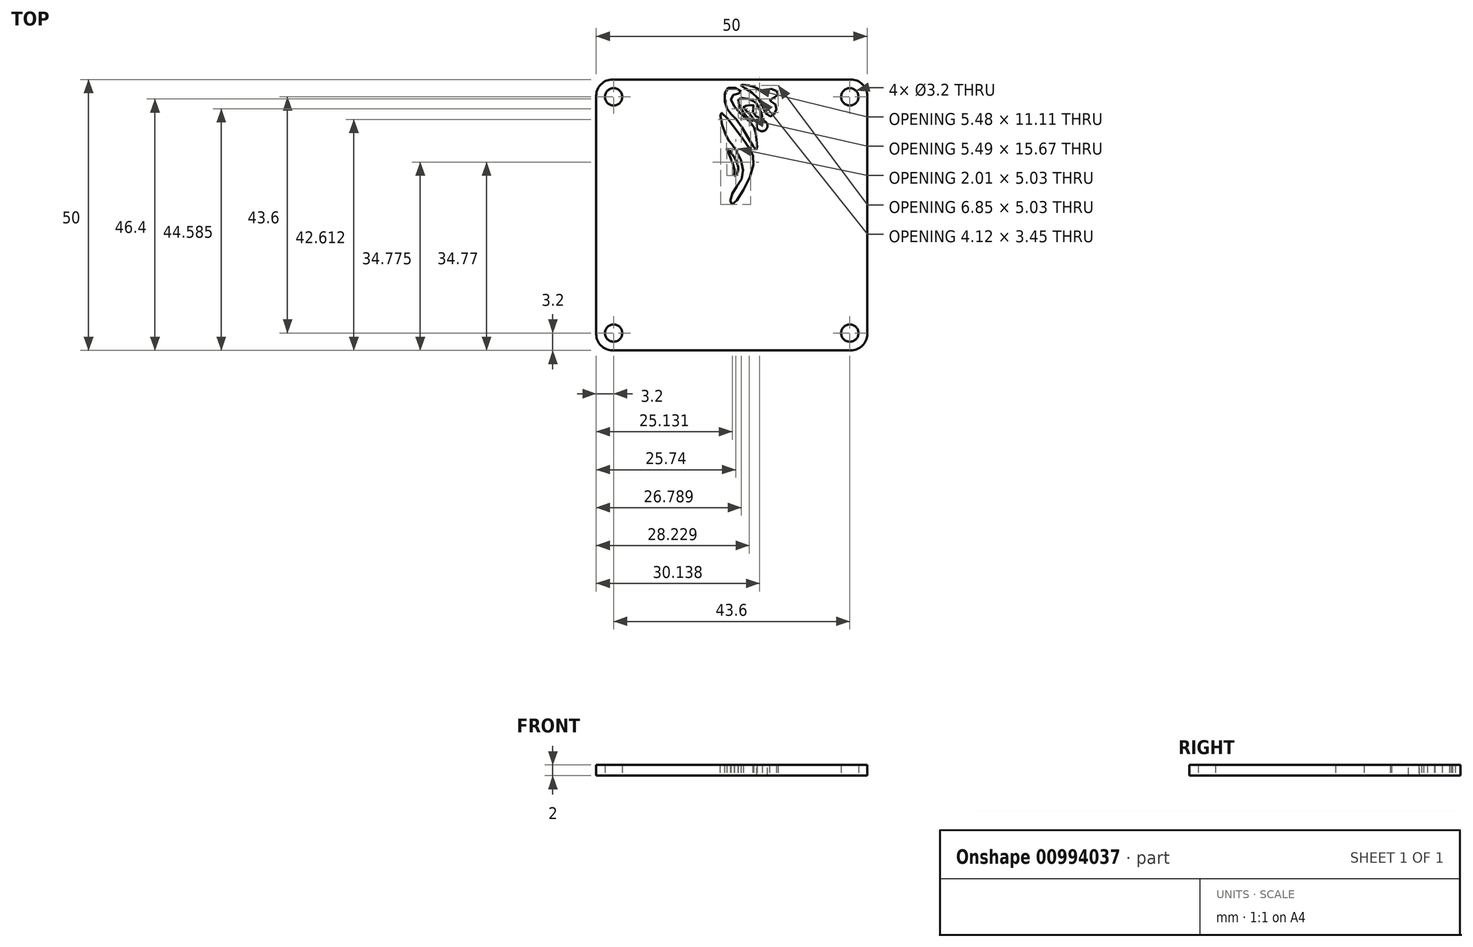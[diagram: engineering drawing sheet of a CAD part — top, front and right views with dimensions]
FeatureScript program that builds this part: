
annotation { "Feature Type Name" : "Feature", "Feature Type Description" : "" }
export const myFeature = defineFeature(function(context is Context, id is Id, definition is map)
    precondition{}
    {
        {
            var Q0;
            Q0=qCreatedBy(makeId("Top.planeOp"),FACE);
            var sketch = newSketch(context, id + "F0", { "sketchPlane" : qUnion([Q0])});
            skLineSegment(sketch, "E0.bottom", {"start": v(-25, 25) * mm, "end": v(25, 25) * mm});
            skLineSegment(sketch, "E0.top", {"start": v(-25, -25) * mm, "end": v(25, -25) * mm});
            skLineSegment(sketch, "E0.left", {"start": v(-25, 25) * mm, "end": v(-25, -25) * mm});
            skLineSegment(sketch, "E0.right", {"start": v(25, 25) * mm, "end": v(25, -25) * mm});
            skPoint(sketch, "E1", {"position": v(0, 25) * mm});
            skPoint(sketch, "E2", {"position": v(25, 0) * mm});
            skPoint(sketch, "E3", {"position": v(-21.8, 21.8) * mm});
            skPoint(sketch, "E4.1.0", {"position": v(-21.8, -21.8) * mm});
            skPoint(sketch, "E4.2.0", {"position": v(21.8, -21.8) * mm});
            skPoint(sketch, "E4.center", {"position": v(0, 0) * mm});
            skPoint(sketch, "E5.0.3.0", {"position": v(21.8, 21.8) * mm});
            skLineSegment(sketch, "E6", {"start": v(0, 25) * mm, "end": v(0, -25) * mm, "construction": true});
            skLineSegment(sketch, "E7", {"start": v(25, 0) * mm, "end": v(-25, 0) * mm, "construction": true});
            skSolve(sketch);
        }
        {
            var Q0;
            Q0=makeQuery(id+"F0.imprint","IMPRINT",FACE,{"disambiguationData":[TD([[makeQuery(id+"F0.imprint","IMPRINT",EDGE,{"derivedFrom":sQuery(id+"F0.wireOp",EDGE,"E0.bottom")}),-1.0]])]});
            extrude(context, id + "F1", {"entities" : qUnion([Q0]), "depth" : 2 * mm, "offsetDistance" : 25 * mm});
        }
        {
            var Q0;
            Q0=sQuery(id+"F0.wireOp",VERTEX,"E3");
            var Q1;
            Q1=sQuery(id+"F0.wireOp",VERTEX,"E5.0.3.0");
            var Q2;
            Q2=sQuery(id+"F0.wireOp",VERTEX,"E4.2.0");
            var Q3;
            Q3=sQuery(id+"F0.wireOp",VERTEX,"E4.1.0");
            var Q4;
            Q4=makeQuery(id+"F1.opExtrude","SWEPT_BODY",BODY,{"disambiguationData":[OSD([sQuery(id+"F0.wireOp",EDGE,"E0.bottom"),sQuery(id+"F0.wireOp",EDGE,"E0.top"),sQuery(id+"F0.wireOp",EDGE,"E0.left"),sQuery(id+"F0.wireOp",EDGE,"E0.right")])]});
            hole(context, id + "F2", {"style" : HoleStyle.SIMPLE, "endStyle" : HoleEndStyle.THROUGH, "oppositeDirection" : true, "standardTappedOrClearance" : lookupTablePath({ "fit" : "Close", "standard" : "ISO", "size" : "M3", "type" : "Clearance" }), "standardBlindInLast" : lookupTablePath({ "fit" : "Close", "standard" : "ISO", "engagement" : "75%", "pitch" : "0.5 mm", "size" : "M3", "type" : "Clearance & tapped" }), "holeDiameter" : 3.2 * mm, "majorDiameter" : 5 * mm, "isTappedThrough" : true, "tappedDepth" : 12 * mm, "tapClearance" : 3, "startFromSketch" : true, "locations" : qUnion([Q0, Q1, Q2, Q3]), "scope" : qUnion([Q4])});
        }
        {
            var Q0;
            Q0=makeQuery(id+"F1.opExtrude","CAP_FACE",FACE,{"disambiguationData":[OSD([sQuery(id+"F0.wireOp",EDGE,"E0.bottom"),sQuery(id+"F0.wireOp",EDGE,"E0.top"),sQuery(id+"F0.wireOp",EDGE,"E0.left"),sQuery(id+"F0.wireOp",EDGE,"E0.right")])],"isStart":false});
            var sketch = newSketch(context, id + "F3", { "sketchPlane" : qUnion([Q0])});
            skFitSpline(sketch, "E8", {"points": [v(0.03, 1.94) * mm, v(3.96, 8.95) * mm, v(2.06, 14.02) * mm, v(-2.07, 18.85) * mm, v(-0.8, 14.09) * mm, v(0, 13.14) * mm, v(2.12, 7.8) * mm, v(0, 3.76) * mm, v(0.03, 1.94) * mm]});
            skFitSpline(sketch, "E9", {"points": [v(4.53, 12.06) * mm, v(1.3, 17.07) * mm, v(-1.05, 20.05) * mm, v(-0.55, 23.48) * mm, v(1.74, 22.72) * mm, v(0, 21.9) * mm, v(1.61, 18.72) * mm, v(3.96, 16.45) * mm, v(4.6, 13.64) * mm, v(4.53, 12.06) * mm]});
            skFitSpline(sketch, "E10", {"points": [v(-0.87, 12.29) * mm, v(1.22, 8.65) * mm, v(0.53, 7.25) * mm, v(0.43, 8.65) * mm, v(-0.87, 12.29) * mm]});
            skPoint(sketch, "E11.0", {"position": v(0, 0) * mm});
            skFitSpline(sketch, "E12", {"points": [v(1.17, 21.3) * mm, v(3.73, 21.15) * mm, v(4.86, 20.08) * mm, v(5.55, 17.89) * mm, v(3.95, 18.85) * mm, v(4.06, 20.19) * mm, v(2.88, 20.19) * mm, v(2.19, 19.87) * mm, v(4, 17.78) * mm, v(3.68, 17.35) * mm, v(1.17, 21.3) * mm]});
            skFitSpline(sketch, "E13", {"points": [v(4.38, 23.55) * mm, v(1.7, 23.98) * mm, v(4.48, 21.95) * mm, v(6.3, 18.85) * mm, v(7.47, 18.26) * mm, v(8.12, 20.35) * mm, v(7, 21.15) * mm, v(8.54, 22.27) * mm, v(7.26, 23.29) * mm, v(5.6, 22.96) * mm, v(4.38, 23.55) * mm]});
            skCircle(sketch, "E14", {"center": v(5.6, 16.45) * mm, "radius": 1 * mm});
            skSolve(sketch);
        }
        {
            var Q0;
            Q0=makeQuery(id+"F3.imprint","IMPRINT",FACE,{"disambiguationData":[TD([[makeQuery(id+"F3.imprint","IMPRINT",EDGE,{"derivedFrom":sQuery(id+"F3.wireOp",EDGE,"E8")}),1.0]])]});
            var Q1;
            Q1=makeQuery(id+"F3.imprint","IMPRINT",FACE,{"disambiguationData":[TD([[makeQuery(id+"F3.imprint","IMPRINT",EDGE,{"derivedFrom":sQuery(id+"F3.wireOp",EDGE,"E9")}),-1.0]])]});
            var Q2;
            Q2=makeQuery(id+"F3.imprint","IMPRINT",FACE,{"disambiguationData":[TD([[makeQuery(id+"F3.imprint","IMPRINT",EDGE,{"derivedFrom":sQuery(id+"F3.wireOp",EDGE,"E10")}),-1.0]])]});
            var Q3;
            Q3=makeQuery(id+"F3.imprint","IMPRINT",FACE,{"disambiguationData":[TD([[makeQuery(id+"F3.imprint","IMPRINT",EDGE,{"derivedFrom":sQuery(id+"F3.wireOp",EDGE,"0e831b12-4cfc-4eb4-9b18-7b789f5edcee")}),1.0]])]});
            var Q4;
            Q4=makeQuery(id+"F3.imprint","IMPRINT",FACE,{"disambiguationData":[TD([[makeQuery(id+"F3.imprint","IMPRINT",EDGE,{"derivedFrom":sQuery(id+"F3.wireOp",EDGE,"E12")}),-1.0]])]});
            var Q5;
            Q5=makeQuery(id+"F3.imprint","IMPRINT",FACE,{"disambiguationData":[TD([[makeQuery(id+"F3.imprint","IMPRINT",EDGE,{"derivedFrom":sQuery(id+"F3.wireOp",EDGE,"E13")}),1.0]])]});
            var Q6;
            Q6=makeQuery(id+"F3.imprint","IMPRINT",FACE,{"disambiguationData":[TD([[makeQuery(id+"F3.imprint","IMPRINT",EDGE,{"derivedFrom":sQuery(id+"F3.wireOp",EDGE,"E14")}),1.0]])]});
            extrude(context, id + "F4", {"entities" : qUnion([Q0, Q1, Q2, Q3, Q4, Q5, Q6]), "operationType" : NewBodyOperationType.REMOVE, "endBound" : BoundingType.THROUGH_ALL, "oppositeDirection" : true, "depth" : 25 * mm, "offsetDistance" : 25 * mm});
        }
        {
            var Q0;
            Q0=qCreatedBy(makeId("Right.planeOp"),FACE);
            var sketch = newSketch(context, id + "F5", { "sketchPlane" : qUnion([Q0])});
            skPoint(sketch, "E15.0", {"position": v(0, 0) * mm});
            skPoint(sketch, "E16.0", {"position": v(0, 2) * mm});
            skLineSegment(sketch, "E17.0", {"start": v(0, 0) * mm, "end": v(0, 2) * mm});
            skSolve(sketch);
        }
        {
            var Q0;
            Q0=makeQuery(id+"F1.opExtrude","SWEPT_EDGE",EDGE,{"disambiguationData":[OSD([sQuery(id+"F0.wireOp",EDGE,"E0.bottom"),sQuery(id+"F0.wireOp",EDGE,"E0.left")])]});
            var Q1;
            Q1=makeQuery(id+"F1.opExtrude","SWEPT_EDGE",EDGE,{"disambiguationData":[OSD([sQuery(id+"F0.wireOp",EDGE,"E0.bottom"),sQuery(id+"F0.wireOp",EDGE,"E0.right")])]});
            var Q2;
            Q2=makeQuery(id+"F1.opExtrude","SWEPT_EDGE",EDGE,{"disambiguationData":[OSD([sQuery(id+"F0.wireOp",EDGE,"E0.top"),sQuery(id+"F0.wireOp",EDGE,"E0.right")])]});
            var Q3;
            Q3=makeQuery(id+"F1.opExtrude","SWEPT_EDGE",EDGE,{"disambiguationData":[OSD([sQuery(id+"F0.wireOp",EDGE,"E0.top"),sQuery(id+"F0.wireOp",EDGE,"E0.left")])]});
            fillet(context, id + "F6", {"entities" : qUnion([Q0, Q1, Q2, Q3]), "radius" : 3 * mm, "tangentPropagation" : true, "allowEdgeOverflow" : false});
        }
    });
